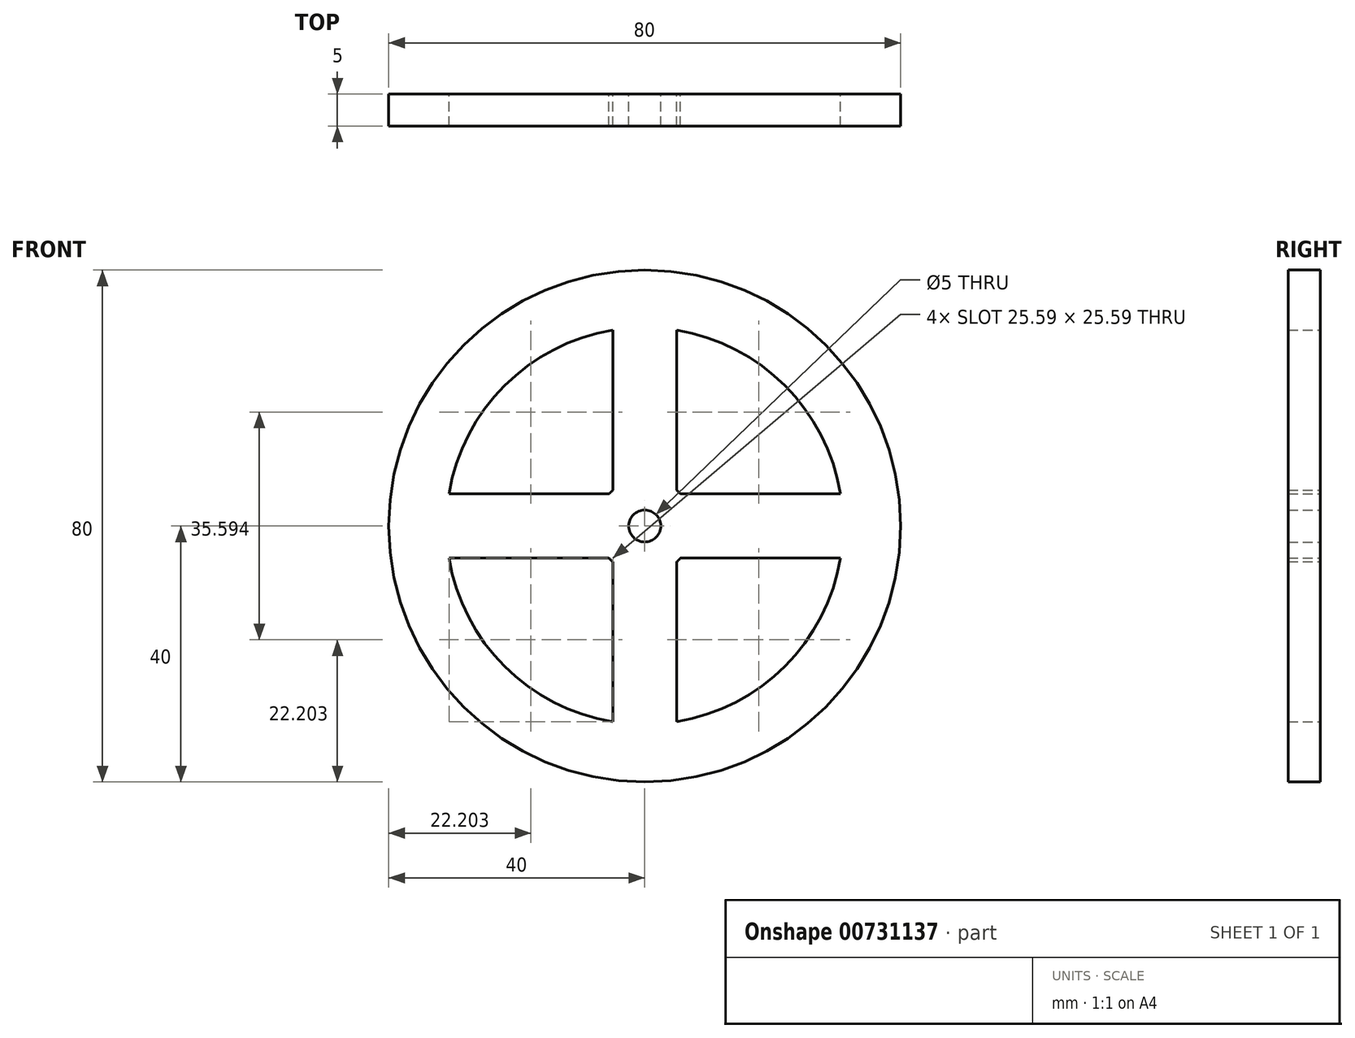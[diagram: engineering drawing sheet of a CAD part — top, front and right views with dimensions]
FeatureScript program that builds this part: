
annotation { "Feature Type Name" : "Feature", "Feature Type Description" : "" }
export const myFeature = defineFeature(function(context is Context, id is Id, definition is map)
    precondition{}
    {
        {
            var Q0;
            Q0=qCreatedBy(makeId("Front.planeOp"),FACE);
            var sketch = newSketch(context, id + "F0", { "sketchPlane" : qUnion([Q0])});
            skCircle(sketch, "E0", {"center": v(0, 0) * mm, "radius": 40 * mm});
            skArc(sketch, "E1", {"start": v(-5, 30.6) * mm, "mid": v(-21.92, 21.92) * mm, "end": v(-30.6, 5) * mm});
            skArc(sketch, "E2", {"start": v(5, -5.6) * mm, "mid": v(5.3, -5.3) * mm, "end": v(5.6, -5) * mm});
            skCircle(sketch, "E3", {"center": v(0, 0) * mm, "radius": 2.5 * mm});
            skLineSegment(sketch, "E4", {"start": v(0, 0) * mm, "end": v(0, 31) * mm, "construction": true});
            skLineSegment(sketch, "E5", {"start": v(0, 0) * mm, "end": v(31, 0) * mm, "construction": true});
            skLineSegment(sketch, "E6", {"start": v(0, 0) * mm, "end": v(0, -31) * mm, "construction": true});
            skLineSegment(sketch, "E7", {"start": v(0, 0) * mm, "end": v(-31, 0) * mm, "construction": true});
            skLineSegment(sketch, "E8.0", {"start": v(-5, 5.6) * mm, "end": v(-5, 30.6) * mm});
            skLineSegment(sketch, "E9.0", {"start": v(5, 5.6) * mm, "end": v(5, 30.6) * mm});
            skLineSegment(sketch, "E10.0", {"start": v(5.6, 5) * mm, "end": v(30.6, 5) * mm});
            skLineSegment(sketch, "E11.0", {"start": v(5.6, -5) * mm, "end": v(30.6, -5) * mm});
            skLineSegment(sketch, "E12.0", {"start": v(5, -5.6) * mm, "end": v(5, -30.6) * mm});
            skLineSegment(sketch, "E13.0", {"start": v(-5, -5.6) * mm, "end": v(-5, -30.6) * mm});
            skLineSegment(sketch, "E14.0", {"start": v(-5.6, -5) * mm, "end": v(-30.6, -5) * mm});
            skLineSegment(sketch, "E15.0", {"start": v(-5.6, 5) * mm, "end": v(-30.6, 5) * mm});
            skArc(sketch, "E16.trimOffspring", {"start": v(-30.6, -5) * mm, "mid": v(-21.92, -21.92) * mm, "end": v(-5, -30.6) * mm});
            skArc(sketch, "E17.trimOffspring", {"start": v(5, -30.6) * mm, "mid": v(21.92, -21.92) * mm, "end": v(30.6, -5) * mm});
            skArc(sketch, "E18.trimOffspring", {"start": v(30.6, 5) * mm, "mid": v(21.92, 21.92) * mm, "end": v(5, 30.6) * mm});
            skArc(sketch, "E19.trimOffspring", {"start": v(5.6, 5) * mm, "mid": v(5.3, 5.3) * mm, "end": v(5, 5.6) * mm});
            skArc(sketch, "E20.trimOffspring", {"start": v(-5.6, -5) * mm, "mid": v(-5.3, -5.3) * mm, "end": v(-5, -5.6) * mm});
            skArc(sketch, "E21.trimOffspring", {"start": v(-5, 5.6) * mm, "mid": v(-5.3, 5.3) * mm, "end": v(-5.6, 5) * mm});
            skSolve(sketch);
        }
        {
            var Q0;
            Q0=makeQuery(id+"F0.imprint","IMPRINT",FACE,{"disambiguationData":[TD([[makeQuery(id+"F0.imprint","IMPRINT",EDGE,{"derivedFrom":sQuery(id+"F0.wireOp",EDGE,"E0")}),1.0]])]});
            extrude(context, id + "F1", {"entities" : qUnion([Q0]), "endBound" : BoundingType.SYMMETRIC, "depth" : 5 * mm, "offsetDistance" : 25 * mm});
        }
    });
